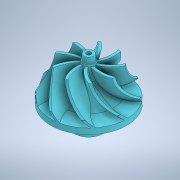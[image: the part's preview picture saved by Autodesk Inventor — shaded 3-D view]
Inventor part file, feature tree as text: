
AUTODESK INVENTOR PART (.ipt)
format: ipt  version: 2022 (Build 260153000, 153)  size: 710,144 bytes
history: native  units: mm
features: sketch x8, extrude x4, revolve x2, plane x2, sweep x1, pattern_circular x1
ambient origin geometry x8: Origin, YZ Plane, XZ Plane, XY Plane, X Axis, Y Axis, Z Axis, Center Point
bodies: Solid1 (feature_tree)
feature tree (18):
  revolve  "Revolution1"  [1 undecoded]
  plane  "Work Plane1"
  sketch  "Sketch3"  dims[d2=20.0mm d3=3.0mm]
  plane  "Work Plane2"
  sweep  "Sweep1"
  pattern_circular  "Circular Pattern1"  [2 undecoded]
  revolve  "Revolution2"  [1 undecoded]
  extrude  "Extrusion2"  Depth=2.5mm
  extrude  "Extrusion3"  Depth=2.5mm
  extrude  "Extrusion4"  Depth=2.5mm
  extrude  "Extrusion5"  Depth=2.5mm
  sketch  "Sketch1"  dims[d0=20.0mm d1=0.0mm]
  sketch  "Sketch4"  dims[d4=3.0mm]
  sketch  "Sketch5"  dims[d5=7.0mm]
  sketch  "Sketch6"  dims[d6=7.0mm]
  sketch  "Sketch7"  dims[d7=0.0mm]
  sketch  "Sketch8"  dims[d8=90.0deg]
  sketch  "Sketch9"  dims[d12=-1.0mm d14=6.981317mm d15=0.625mm d16=0.625mm d17=16.918mm d18=16.918mm d19=0.625mm d20=0.625mm d21=0.0mm d22=0.0mm d23=90.0mm d24=360.0deg d26=6.5mm d27=10.0mm d28=4.0mm d32=360.0deg d34=15.0mm d35=10.0mm d36=0.0mm d37=5.0mm d38=3.0mm d39=0.0mm d40=2.4mm d41=35.0mm d42=0.0mm d43=2.8mm d44=2.5mm d45=0.0mm d46=0.0mm d47=0.0mm d48=0.0mm d33=0.872665mm]
note: 4 required parameter values undecoded (feature->parameter linkage not recoverable at this tier; creation-order binding heuristic only, values carry confidence <= 0.55)